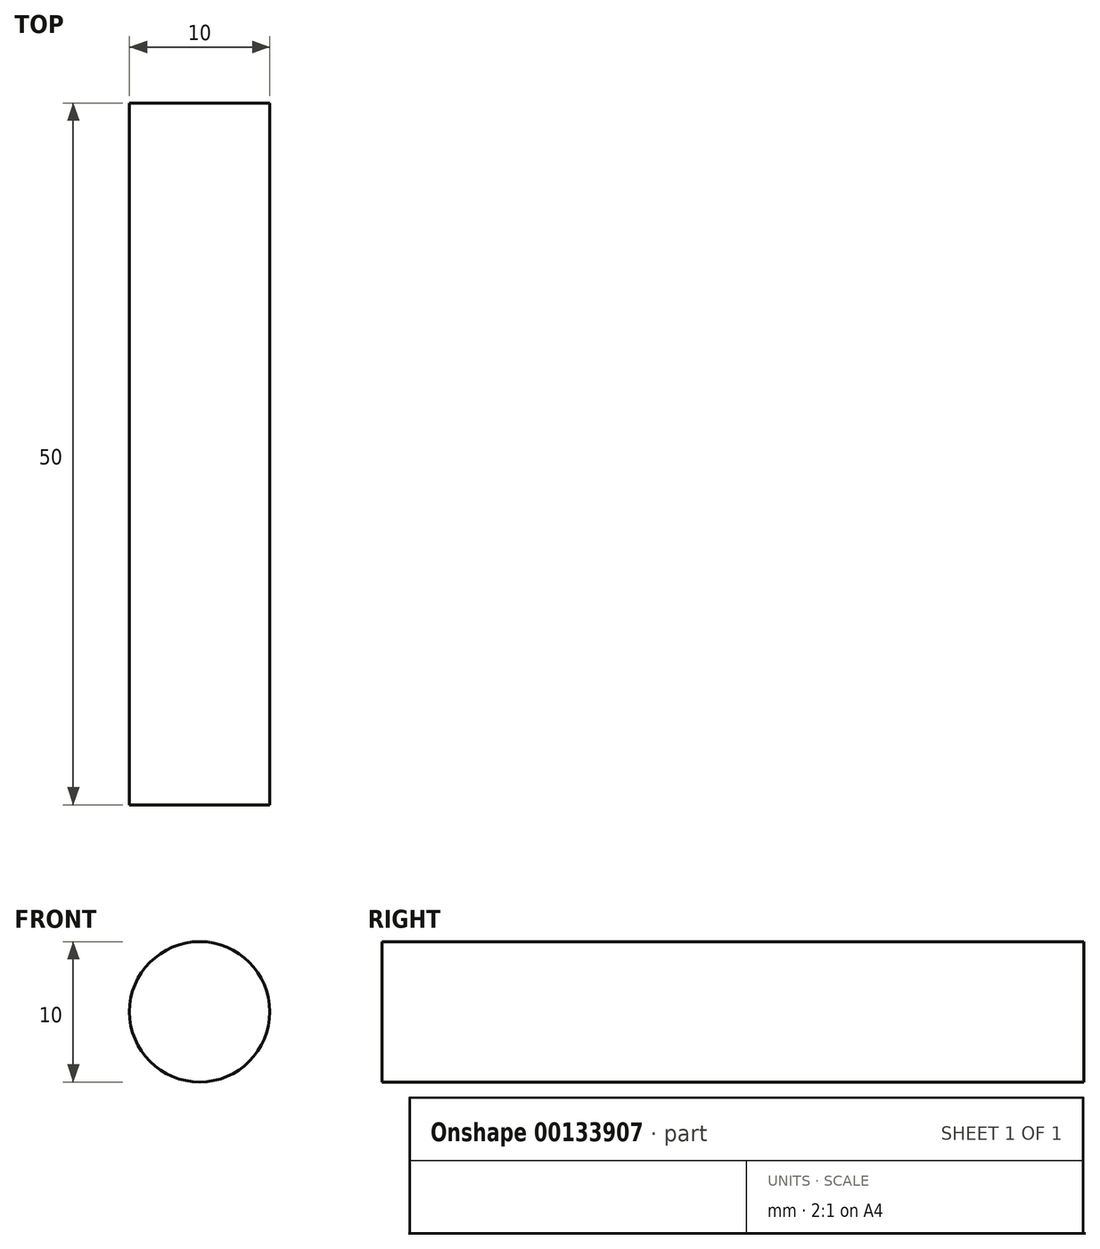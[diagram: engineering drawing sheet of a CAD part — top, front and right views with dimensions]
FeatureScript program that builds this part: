
annotation { "Feature Type Name" : "Feature", "Feature Type Description" : "" }
export const myFeature = defineFeature(function(context is Context, id is Id, definition is map)
    precondition{}
    {
        {
            var Q0;
            Q0=qCreatedBy(makeId("Front.planeOp"),FACE);
            var sketch = newSketch(context, id + "F0", { "sketchPlane" : qUnion([Q0])});
            skCircle(sketch, "E0", {"center": v(0, 0) * mm, "radius": 5 * mm});
            skSolve(sketch);
        }
        {
            var Q0;
            Q0=makeQuery(id+"F0.imprint","IMPRINT",FACE,{"disambiguationData":[TD([[makeQuery(id+"F0.imprint","IMPRINT",EDGE,{"derivedFrom":sQuery(id+"F0.wireOp",EDGE,"E0")}),1.0]])]});
            extrude(context, id + "F1", {"entities" : qUnion([Q0]), "depth" : 50 * mm});
        }
    });
